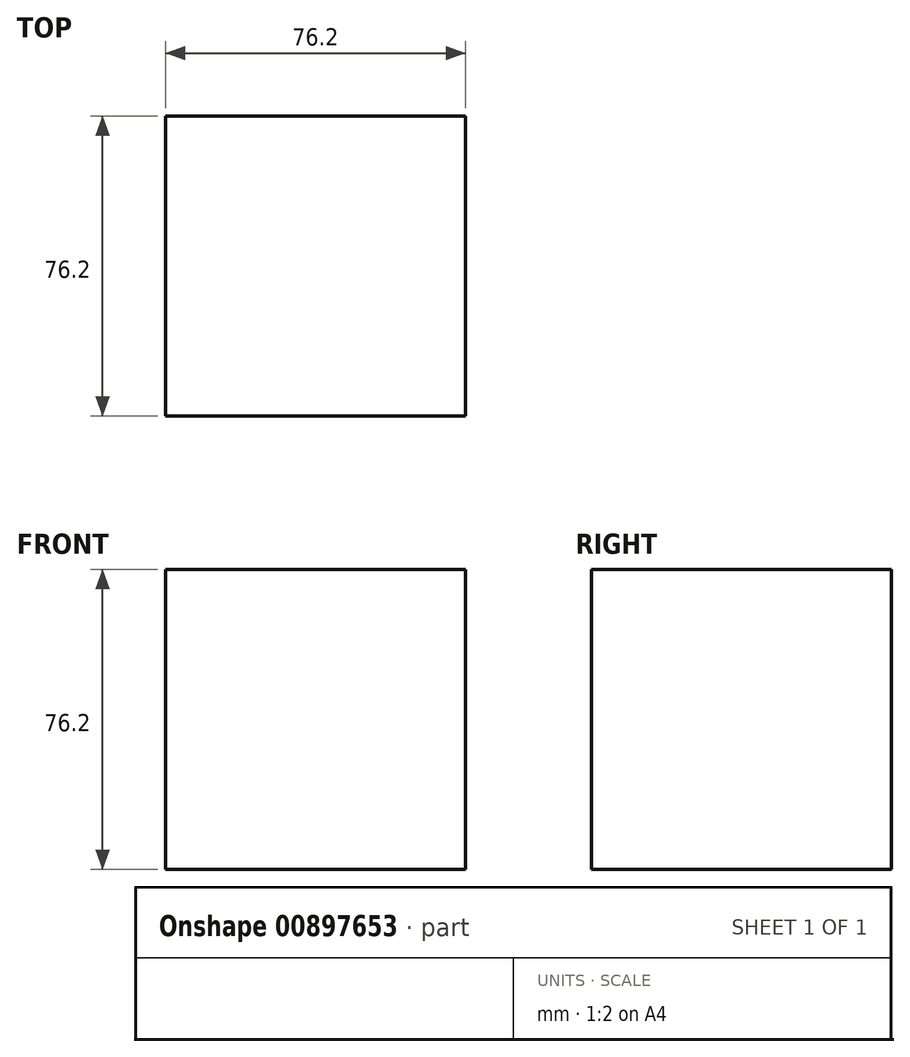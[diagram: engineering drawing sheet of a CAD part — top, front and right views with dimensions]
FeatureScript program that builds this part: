
annotation { "Feature Type Name" : "Feature", "Feature Type Description" : "" }
export const myFeature = defineFeature(function(context is Context, id is Id, definition is map)
    precondition{}
    {
        {
            var Q0;
            Q0=qCreatedBy(makeId("Front.planeOp"),FACE);
            var sketch = newSketch(context, id + "F0", { "sketchPlane" : qUnion([Q0])});
            skLineSegment(sketch, "E0.bottom", {"start": v(38.1, 38.1) * mm, "end": v(-38.1, 38.1) * mm});
            skLineSegment(sketch, "E0.top", {"start": v(38.1, -38.1) * mm, "end": v(-38.1, -38.1) * mm});
            skLineSegment(sketch, "E0.left", {"start": v(38.1, 38.1) * mm, "end": v(38.1, -38.1) * mm});
            skLineSegment(sketch, "E0.right", {"start": v(-38.1, 38.1) * mm, "end": v(-38.1, -38.1) * mm});
            skPoint(sketch, "E0.middle", {"position": v(0, 0) * mm});
            skSolve(sketch);
        }
        {
            var Q0;
            Q0 = qSketchRegion(id + "F0", true);
            extrude(context, id + "F1", {"entities" : qUnion([Q0]), "depth" : 76.2 * mm, "offsetDistance" : 25.4 * mm});
        }
    });
